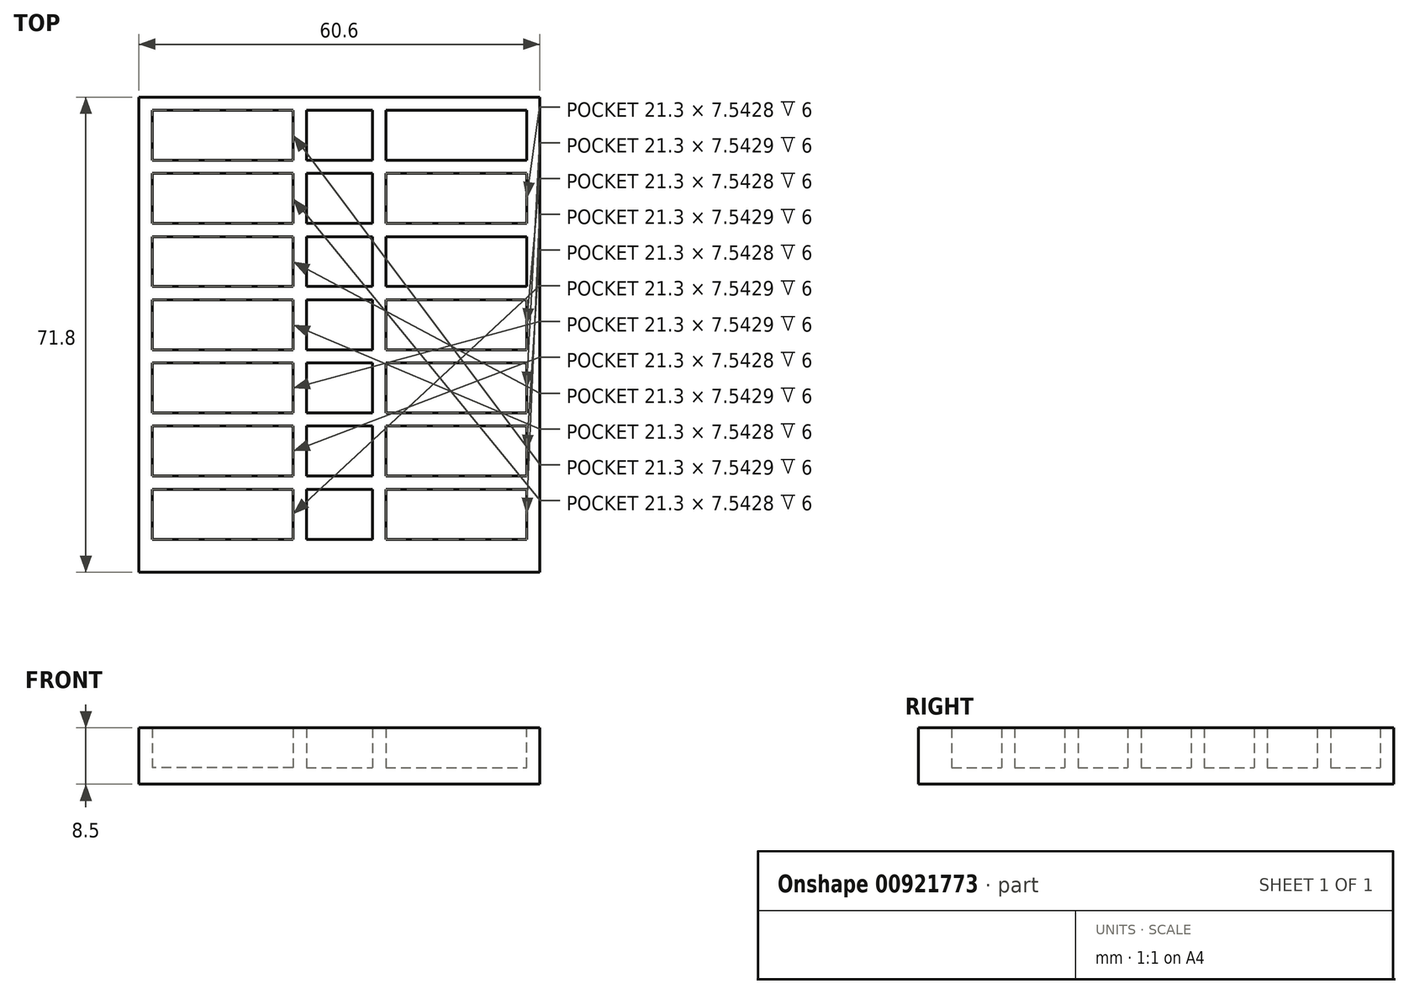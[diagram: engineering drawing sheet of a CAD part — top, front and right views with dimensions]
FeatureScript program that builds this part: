
annotation { "Feature Type Name" : "Feature", "Feature Type Description" : "" }
export const myFeature = defineFeature(function(context is Context, id is Id, definition is map)
    precondition{}
    {
        {
            var Q0;
            Q0=qCreatedBy(makeId("Top.planeOp"),FACE);
            var sketch = newSketch(context, id + "F0", { "sketchPlane" : qUnion([Q0])});
            skLineSegment(sketch, "E0.bottom", {"start": v(0, 0) * mm, "end": v(60.6, 0) * mm});
            skLineSegment(sketch, "E0.top", {"start": v(0, 71.8) * mm, "end": v(60.6, 71.8) * mm});
            skLineSegment(sketch, "E0.left", {"start": v(0, 0) * mm, "end": v(0, 71.8) * mm});
            skLineSegment(sketch, "E0.right", {"start": v(60.6, 0) * mm, "end": v(60.6, 71.8) * mm});
            skSolve(sketch);
        }
        {
            var Q0;
            Q0 = qSketchRegion(id + "F0", true);
            extrude(context, id + "F1", {"entities" : qUnion([Q0]), "depth" : 8.5 * mm, "offsetDistance" : 25 * mm});
        }
        {
            var Q0;
            Q0=makeQuery(id+"F1.opExtrude","CAP_FACE",FACE,{"disambiguationData":[OSD([sQuery(id+"F0.wireOp",EDGE,"E0.bottom"),sQuery(id+"F0.wireOp",EDGE,"E0.top"),sQuery(id+"F0.wireOp",EDGE,"E0.left"),sQuery(id+"F0.wireOp",EDGE,"E0.right")])],"isStart":false});
            var sketch = newSketch(context, id + "F2", { "sketchPlane" : qUnion([Q0])});
            skLineSegment(sketch, "E1.0", {"start": v(2, 69.8) * mm, "end": v(58.6, 69.8) * mm});
            skLineSegment(sketch, "E2.0", {"start": v(58.6, 5) * mm, "end": v(58.6, 69.8) * mm});
            skLineSegment(sketch, "E3.0", {"start": v(2, 5) * mm, "end": v(2, 69.8) * mm});
            skLineSegment(sketch, "E4.0", {"start": v(2, 5) * mm, "end": v(58.6, 5) * mm});
            skSolve(sketch);
        }
        {
            var Q0;
            Q0 = qSketchRegion(id + "F2", true);
            extrude(context, id + "F3", {"entities" : qUnion([Q0]), "operationType" : NewBodyOperationType.REMOVE, "oppositeDirection" : true, "depth" : 6 * mm, "offsetDistance" : 25 * mm});
        }
        {
            var Q0;
            Q0=makeQuery(id+"F3.boolean.opBoolean","COPY",FACE,{"derivedFrom":makeQuery(id+"F3.opExtrude","CAP_FACE",FACE,{"disambiguationData":[OSD([sQuery(id+"F2.wireOp",EDGE,"E1.0"),sQuery(id+"F2.wireOp",EDGE,"E2.0"),sQuery(id+"F2.wireOp",EDGE,"E3.0"),sQuery(id+"F2.wireOp",EDGE,"E4.0")])],"isStart":false})});
            var sketch = newSketch(context, id + "F4", { "sketchPlane" : qUnion([Q0])});
            skLineSegment(sketch, "E5.bottom", {"start": v(23.3, 69.8) * mm, "end": v(25.3, 69.8) * mm});
            skLineSegment(sketch, "E5.top", {"start": v(23.3, 5) * mm, "end": v(25.3, 5) * mm});
            skLineSegment(sketch, "E5.left", {"start": v(23.3, 69.8) * mm, "end": v(23.3, 62.26) * mm});
            skLineSegment(sketch, "E5.right", {"start": v(25.3, 69.8) * mm, "end": v(25.3, 62.26) * mm});
            skLineSegment(sketch, "E6.bottom", {"start": v(35.3, 69.8) * mm, "end": v(37.3, 69.8) * mm});
            skLineSegment(sketch, "E6.top", {"start": v(35.3, 5) * mm, "end": v(37.3, 5) * mm});
            skLineSegment(sketch, "E6.left", {"start": v(35.3, 69.8) * mm, "end": v(35.3, 62.26) * mm});
            skLineSegment(sketch, "E6.right", {"start": v(37.3, 69.8) * mm, "end": v(37.3, 62.26) * mm});
            skLineSegment(sketch, "E7", {"start": v(58.6, 69.8) * mm, "end": v(58.6, 5) * mm, "construction": true});
            skLineSegment(sketch, "E8", {"start": v(58.6, 5) * mm, "end": v(2, 5) * mm, "construction": true});
            skLineSegment(sketch, "E9.bottom", {"start": v(2, 62.26) * mm, "end": v(23.3, 62.26) * mm});
            skLineSegment(sketch, "E9.top", {"start": v(2, 60.26) * mm, "end": v(23.3, 60.26) * mm});
            skLineSegment(sketch, "E9.left", {"start": v(2, 62.26) * mm, "end": v(2, 60.26) * mm});
            skLineSegment(sketch, "E9.right", {"start": v(58.6, 62.26) * mm, "end": v(58.6, 60.26) * mm});
            skLineSegment(sketch, "E10.bottom", {"start": v(58.6, 52.71) * mm, "end": v(37.3, 52.71) * mm});
            skLineSegment(sketch, "E10.top", {"start": v(58.6, 50.71) * mm, "end": v(37.3, 50.71) * mm});
            skLineSegment(sketch, "E10.left", {"start": v(58.6, 52.71) * mm, "end": v(58.6, 50.71) * mm});
            skLineSegment(sketch, "E10.right", {"start": v(2, 52.71) * mm, "end": v(2, 50.71) * mm});
            skLineSegment(sketch, "E11.bottom", {"start": v(2, 43.17) * mm, "end": v(23.3, 43.17) * mm});
            skLineSegment(sketch, "E11.top", {"start": v(2, 41.17) * mm, "end": v(23.3, 41.17) * mm});
            skLineSegment(sketch, "E11.left", {"start": v(2, 43.17) * mm, "end": v(2, 41.17) * mm});
            skLineSegment(sketch, "E11.right", {"start": v(58.6, 43.17) * mm, "end": v(58.6, 41.17) * mm});
            skLineSegment(sketch, "E12.bottom", {"start": v(58.6, 33.63) * mm, "end": v(37.3, 33.63) * mm});
            skLineSegment(sketch, "E12.top", {"start": v(58.6, 31.63) * mm, "end": v(37.3, 31.63) * mm});
            skLineSegment(sketch, "E12.left", {"start": v(58.6, 33.63) * mm, "end": v(58.6, 31.63) * mm});
            skLineSegment(sketch, "E12.right", {"start": v(2, 33.63) * mm, "end": v(2, 31.63) * mm});
            skLineSegment(sketch, "E13.bottom", {"start": v(2, 24.09) * mm, "end": v(23.3, 24.09) * mm});
            skLineSegment(sketch, "E13.top", {"start": v(2, 22.09) * mm, "end": v(23.3, 22.09) * mm});
            skLineSegment(sketch, "E13.left", {"start": v(2, 24.09) * mm, "end": v(2, 22.09) * mm});
            skLineSegment(sketch, "E13.right", {"start": v(58.6, 24.09) * mm, "end": v(58.6, 22.09) * mm});
            skLineSegment(sketch, "E14.bottom", {"start": v(58.6, 14.54) * mm, "end": v(37.3, 14.54) * mm});
            skLineSegment(sketch, "E14.top", {"start": v(58.6, 12.54) * mm, "end": v(37.3, 12.54) * mm});
            skLineSegment(sketch, "E14.left", {"start": v(58.6, 14.54) * mm, "end": v(58.6, 12.54) * mm});
            skLineSegment(sketch, "E14.right", {"start": v(2, 14.54) * mm, "end": v(2, 12.54) * mm});
            skLineSegment(sketch, "E15.trimOffspring", {"start": v(25.3, 62.26) * mm, "end": v(35.3, 62.26) * mm});
            skLineSegment(sketch, "E16.trimOffspring", {"start": v(23.3, 60.26) * mm, "end": v(23.3, 52.71) * mm});
            skLineSegment(sketch, "E17.trimOffspring", {"start": v(25.3, 60.26) * mm, "end": v(35.3, 60.26) * mm});
            skLineSegment(sketch, "E18.trimOffspring", {"start": v(25.3, 60.26) * mm, "end": v(25.3, 52.71) * mm});
            skLineSegment(sketch, "E19.trimOffspring", {"start": v(35.3, 60.26) * mm, "end": v(35.3, 52.71) * mm});
            skLineSegment(sketch, "E20.trimOffspring", {"start": v(37.3, 62.26) * mm, "end": v(58.6, 62.26) * mm});
            skLineSegment(sketch, "E21.trimOffspring", {"start": v(37.3, 60.26) * mm, "end": v(37.3, 52.71) * mm});
            skLineSegment(sketch, "E22.trimOffspring", {"start": v(37.3, 60.26) * mm, "end": v(58.6, 60.26) * mm});
            skLineSegment(sketch, "E23.trimOffspring", {"start": v(35.3, 52.71) * mm, "end": v(25.3, 52.71) * mm});
            skLineSegment(sketch, "E24.trimOffspring", {"start": v(35.3, 50.71) * mm, "end": v(25.3, 50.71) * mm});
            skLineSegment(sketch, "E25.trimOffspring", {"start": v(35.3, 50.71) * mm, "end": v(35.3, 43.17) * mm});
            skLineSegment(sketch, "E26.trimOffspring", {"start": v(37.3, 50.71) * mm, "end": v(37.3, 43.17) * mm});
            skLineSegment(sketch, "E27.trimOffspring", {"start": v(25.3, 50.71) * mm, "end": v(25.3, 43.17) * mm});
            skLineSegment(sketch, "E28.trimOffspring", {"start": v(23.3, 52.71) * mm, "end": v(2, 52.71) * mm});
            skLineSegment(sketch, "E29.trimOffspring", {"start": v(23.3, 50.71) * mm, "end": v(23.3, 43.17) * mm});
            skLineSegment(sketch, "E30.trimOffspring", {"start": v(23.3, 50.71) * mm, "end": v(2, 50.71) * mm});
            skLineSegment(sketch, "E31.trimOffspring", {"start": v(25.3, 43.17) * mm, "end": v(35.3, 43.17) * mm});
            skLineSegment(sketch, "E32.trimOffspring", {"start": v(23.3, 41.17) * mm, "end": v(23.3, 33.63) * mm});
            skLineSegment(sketch, "E33.trimOffspring", {"start": v(25.3, 41.17) * mm, "end": v(35.3, 41.17) * mm});
            skLineSegment(sketch, "E34.trimOffspring", {"start": v(25.3, 41.17) * mm, "end": v(25.3, 33.63) * mm});
            skLineSegment(sketch, "E35.trimOffspring", {"start": v(35.3, 41.17) * mm, "end": v(35.3, 33.63) * mm});
            skLineSegment(sketch, "E36.trimOffspring", {"start": v(37.3, 43.17) * mm, "end": v(58.6, 43.17) * mm});
            skLineSegment(sketch, "E37.trimOffspring", {"start": v(37.3, 41.17) * mm, "end": v(37.3, 33.63) * mm});
            skLineSegment(sketch, "E38.trimOffspring", {"start": v(37.3, 41.17) * mm, "end": v(58.6, 41.17) * mm});
            skLineSegment(sketch, "E39.trimOffspring", {"start": v(35.3, 33.63) * mm, "end": v(25.3, 33.63) * mm});
            skLineSegment(sketch, "E40.trimOffspring", {"start": v(35.3, 31.63) * mm, "end": v(25.3, 31.63) * mm});
            skLineSegment(sketch, "E41.trimOffspring", {"start": v(37.3, 31.63) * mm, "end": v(37.3, 24.09) * mm});
            skLineSegment(sketch, "E42.trimOffspring", {"start": v(35.3, 31.63) * mm, "end": v(35.3, 24.09) * mm});
            skLineSegment(sketch, "E43.trimOffspring", {"start": v(25.3, 31.63) * mm, "end": v(25.3, 24.09) * mm});
            skLineSegment(sketch, "E44.trimOffspring", {"start": v(23.3, 33.63) * mm, "end": v(2, 33.63) * mm});
            skLineSegment(sketch, "E45.trimOffspring", {"start": v(23.3, 31.63) * mm, "end": v(23.3, 24.09) * mm});
            skLineSegment(sketch, "E46.trimOffspring", {"start": v(23.3, 31.63) * mm, "end": v(2, 31.63) * mm});
            skLineSegment(sketch, "E47.trimOffspring", {"start": v(25.3, 24.09) * mm, "end": v(35.3, 24.09) * mm});
            skLineSegment(sketch, "E48.trimOffspring", {"start": v(23.3, 22.09) * mm, "end": v(23.3, 14.54) * mm});
            skLineSegment(sketch, "E49.trimOffspring", {"start": v(25.3, 22.09) * mm, "end": v(35.3, 22.09) * mm});
            skLineSegment(sketch, "E50.trimOffspring", {"start": v(25.3, 22.09) * mm, "end": v(25.3, 14.54) * mm});
            skLineSegment(sketch, "E51.trimOffspring", {"start": v(35.3, 22.09) * mm, "end": v(35.3, 14.54) * mm});
            skLineSegment(sketch, "E52.trimOffspring", {"start": v(37.3, 24.09) * mm, "end": v(58.6, 24.09) * mm});
            skLineSegment(sketch, "E53.trimOffspring", {"start": v(37.3, 22.09) * mm, "end": v(37.3, 14.54) * mm});
            skLineSegment(sketch, "E54.trimOffspring", {"start": v(37.3, 22.09) * mm, "end": v(58.6, 22.09) * mm});
            skLineSegment(sketch, "E55.trimOffspring", {"start": v(35.3, 14.54) * mm, "end": v(25.3, 14.54) * mm});
            skLineSegment(sketch, "E56.trimOffspring", {"start": v(37.3, 12.54) * mm, "end": v(37.3, 5) * mm});
            skLineSegment(sketch, "E57.trimOffspring", {"start": v(35.3, 12.54) * mm, "end": v(25.3, 12.54) * mm});
            skLineSegment(sketch, "E58.trimOffspring", {"start": v(35.3, 12.54) * mm, "end": v(35.3, 5) * mm});
            skLineSegment(sketch, "E59.trimOffspring", {"start": v(23.3, 14.54) * mm, "end": v(2, 14.54) * mm});
            skLineSegment(sketch, "E60.trimOffspring", {"start": v(25.3, 12.54) * mm, "end": v(25.3, 5) * mm});
            skLineSegment(sketch, "E61.trimOffspring", {"start": v(23.3, 12.54) * mm, "end": v(2, 12.54) * mm});
            skLineSegment(sketch, "E62.trimOffspring", {"start": v(23.3, 12.54) * mm, "end": v(23.3, 5) * mm});
            skSolve(sketch);
        }
        {
            var Q0;
            Q0 = qSketchRegion(id + "F4", true);
            extrude(context, id + "F5", {"entities" : qUnion([Q0]), "operationType" : NewBodyOperationType.ADD, "depth" : 6 * mm, "offsetDistance" : 25 * mm});
        }
        {
            var Q0;
            Q0=makeQuery(id+"F1.opExtrude","SWEPT_BODY",BODY,{"disambiguationData":[OSD([sQuery(id+"F0.wireOp",EDGE,"E0.bottom"),sQuery(id+"F0.wireOp",EDGE,"E0.top"),sQuery(id+"F0.wireOp",EDGE,"E0.left"),sQuery(id+"F0.wireOp",EDGE,"E0.right")])]});
            transform(context, id + "F6", {"entities" : qUnion([Q0]), "transformType" : TransformType.TRANSLATION_3D, "dx" : 0 * mm, "dy" : 0 * mm, "dz" : 0 * mm, "makeCopy" : true});
        }
        {
            var Q0;
            Q0=makeQuery(id+"F6.opPattern","COPY",BODY,{"derivedFrom":makeQuery(id+"F1.opExtrude","SWEPT_BODY",BODY,{"disambiguationData":[OSD([sQuery(id+"F0.wireOp",EDGE,"E0.bottom"),sQuery(id+"F0.wireOp",EDGE,"E0.top"),sQuery(id+"F0.wireOp",EDGE,"E0.left"),sQuery(id+"F0.wireOp",EDGE,"E0.right")])]}),"instanceName":"1"});
            deleteBodies(context, id + "F7", {"entities" : qUnion([Q0])});
        }
    });
